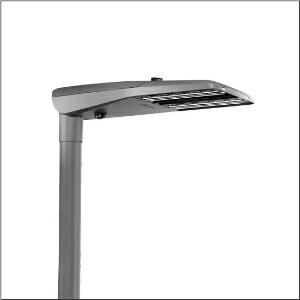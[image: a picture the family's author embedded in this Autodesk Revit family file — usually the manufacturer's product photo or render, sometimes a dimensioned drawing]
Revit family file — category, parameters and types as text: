
# Revit family: streetlight_sl_11_iq_midi___st1_0ab_5xc3n51y08le_be24
name_source: partatom
category: Lighting Fixtures
units: mm (PartAtom-declared; Revit-internal decimal feet)

## family parameters
Cut with Voids When Loaded = No
Host = Face
Light Source = No
Part Type = Normal
Room Calculation Point = No
Round Connector Dimension = Use Diameter
Shared = No

## types (1)
- --- (1 x LED, 7760 lm, 59.4 W, 3000K)
    Apparent Load = 59 VA
    CIE Flux Codes = 29 63 95 100 100
    Color Rendering = 70
    Color Temperature = 3000K
    Default Elevation = 1800 mm
    Description = Streetlight SL 11 iQ midi, mast luminaire, primary light control with 3 zone facetted reflector, of plastic, silver coated, highly specular, primary optical cover: cover, of PMMA, transparent, light distribution: ST1.0aB, light emission: direct distribution, primary light characteristic: asymmetric, installation type: post-top, side-entry, LED, High Power LED, rated luminous flux: 7.760lm, luminous efficacy: 131lm/W, light colour: 730, colour temperature: 3000K, control: presetting dimming logarithmic, Street-Remote, Auto-Match, Temp-Guard, Lumen-Switch, Night-Set, Smart-Wire, Light-Fading, Desk-Remote (wireless, voltage-free reading and setting of iQ features in the workshop via application-optimized NFC function/RFID function), optimised constant luminous flux control (CLO 2.0), with cable H07RN-F 5x 1.5mm², mains connection: 230..240V, AC, 50/60Hz, connection cable pre-assembled, cable length: 8,5m, start of lifetime: 59W, end of service life: 62W, reduction: 29W, luminaire housing, of diecast aluminium, powder-coated, Siteco® metallic grey (DB 702S), please order mast flange separately, inclination adjustable without tools: 0°, 5°, 10°, 15° (post-top) | 0°, -5°, -10°, -15° (side-entry), sealing non-destructively replaceable, multi-level sealing system, length: 780mm, width: 376mm, height: 118mm, mast flange for spigot size: 42mm (side-entry): 5XC10008XM4, 60/48mm (side-entry/post-top): 5XC10108XM2, 76/60mm (side-entry/post-top): 5XC10108XM1, equipment: standard, Smart Interface below and above, protection rating (complete): IP66, insulation class (complete): insulation class II (safety insulation), certification: CE, ENEC, VDE, UKCA, impact resistance: IK09, permissible operating ambient temperature for outdoor applications: -25..+50°C, standard-compliant lighting for roads and squares, Environmental Product Declaration (EPD) tested and certified by an independent institute, packaging unit: 1 piece

Light Distribution: ST1.0aB
    Height = 118 mm
    Lamp = 1 x LED
    Lamp Light Flux = 7760 lm
    Lamp Power = 59.4 W
    Lamp count = 1
    Length = 780 mm
    Luminous efficacy = 131 lm/W
    Manufacturer = Siteco
    ModVariant = No
    Model = 5XC3N51Y08LE
    Number of Poles = 1
    OnlyDefault = Yes
    Power Factor = 1
    Product Name = Streetlight SL 11 iQ midi | ST1.0aB
    Product group = mast luminaire | pylon top
    ProductGroupID = 6100
    Protection Class = Protection class II
    Protection Degree = IP 66
    RLX_Detail_Level = 1
    RLX_Emergency_Light_Flux = 0 lm
    RLX_Emergency_Type = 0
    RLX_Emergency_Type_DB = No
    RlxData = <blob elided: 69001 chars, md5=78bd3a8b>
    Socket = socket
    Standby Power = 0 W
    System Light Flux = 7760 lm
    System Power = 59 W
    Type Comments = factory setting: luminous flux: 100 % | dim-lin: 254 | 521 mA
    Type Image = l_1004429.jpg
    URL = http://relux.com
    VarID = @adj_020107
    Voltage = 0 V
    Weight = 0.00 kg
    Width = 376 mm

## geometry (parser evidence)
native form markers: Blend x4, Sweep x10
no freeform markers — native parametric forms only
